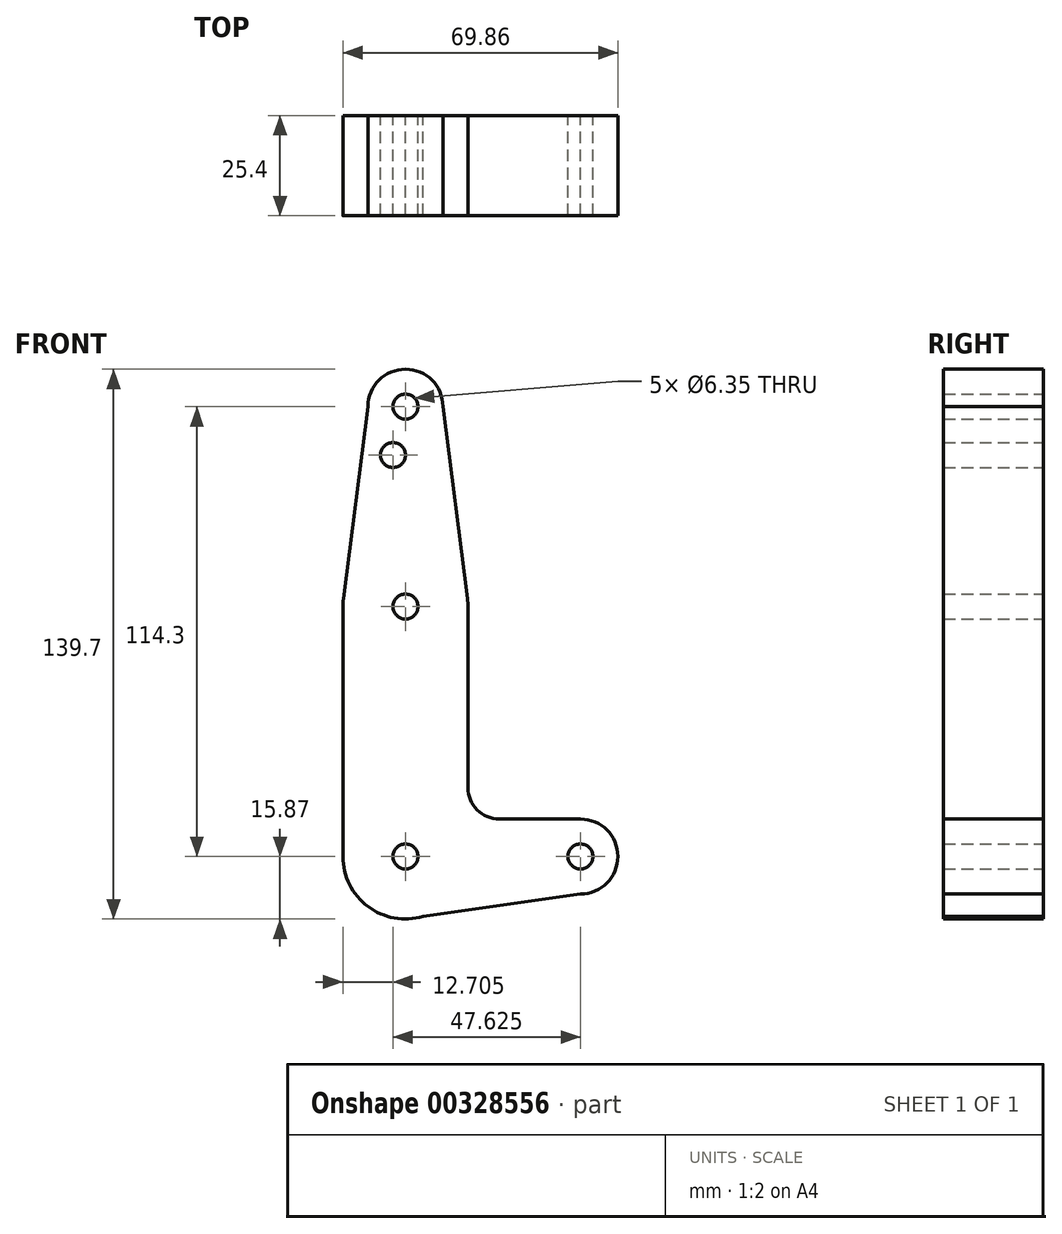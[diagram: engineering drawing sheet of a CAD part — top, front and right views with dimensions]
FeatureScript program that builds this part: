
annotation { "Feature Type Name" : "Feature", "Feature Type Description" : "" }
export const myFeature = defineFeature(function(context is Context, id is Id, definition is map)
    precondition{}
    {
        {
            var Q0;
            Q0=qCreatedBy(makeId("Front.planeOp"),FACE);
            var sketch = newSketch(context, id + "F0", { "sketchPlane" : qUnion([Q0])});
            skLineSegment(sketch, "E0", {"start": v(0, 0) * mm, "end": v(0, 114.3) * mm, "construction": true});
            skLineSegment(sketch, "E1", {"start": v(0, 0) * mm, "end": v(44.45, 0) * mm, "construction": true});
            skCircle(sketch, "E2", {"center": v(0, 114.3) * mm, "radius": 9.53 * mm});
            skCircle(sketch, "E3", {"center": v(0, 63.5) * mm, "radius": 15.88 * mm});
            skCircle(sketch, "E4", {"center": v(0, 0) * mm, "radius": 15.88 * mm});
            skLineSegment(sketch, "E5", {"start": v(-9.53, 114.3) * mm, "end": v(-15.75, 65.5) * mm});
            skLineSegment(sketch, "E6", {"start": v(9.53, 114.3) * mm, "end": v(15.75, 65.5) * mm});
            skLineSegment(sketch, "E7", {"start": v(15.88, 63.5) * mm, "end": v(15.88, 17.48) * mm});
            skLineSegment(sketch, "E8", {"start": v(-15.88, 0) * mm, "end": v(-15.87, 63.5) * mm});
            skLineSegment(sketch, "E9", {"start": v(23.83, 9.52) * mm, "end": v(44.45, 9.53) * mm});
            skCircle(sketch, "E10", {"center": v(0, 114.3) * mm, "radius": 3.18 * mm});
            skCircle(sketch, "E11", {"center": v(0, 63.5) * mm, "radius": 3.18 * mm});
            skCircle(sketch, "E12", {"center": v(0, 0) * mm, "radius": 3.18 * mm});
            skCircle(sketch, "E13", {"center": v(44.45, 0) * mm, "radius": 3.18 * mm});
            skCircle(sketch, "E14", {"center": v(44.45, 0) * mm, "radius": 9.53 * mm});
            skLineSegment(sketch, "E15", {"start": v(0, -15.88) * mm, "end": v(44.45, -9.52) * mm});
            skArc(sketch, "E16.filletArc", {"start": v(15.87, 17.48) * mm, "mid": v(18.2, 11.85) * mm, "end": v(23.83, 9.52) * mm});
            skCircle(sketch, "E17", {"center": v(-3.18, 102) * mm, "radius": 3.18 * mm});
            skSolve(sketch);
        }
        {
            var Q0;
            Q0 = qSketchRegion(id + "F0", true);
            extrude(context, id + "F1", {"entities" : qUnion([Q0]), "depth" : 25.4 * mm});
        }
    });
